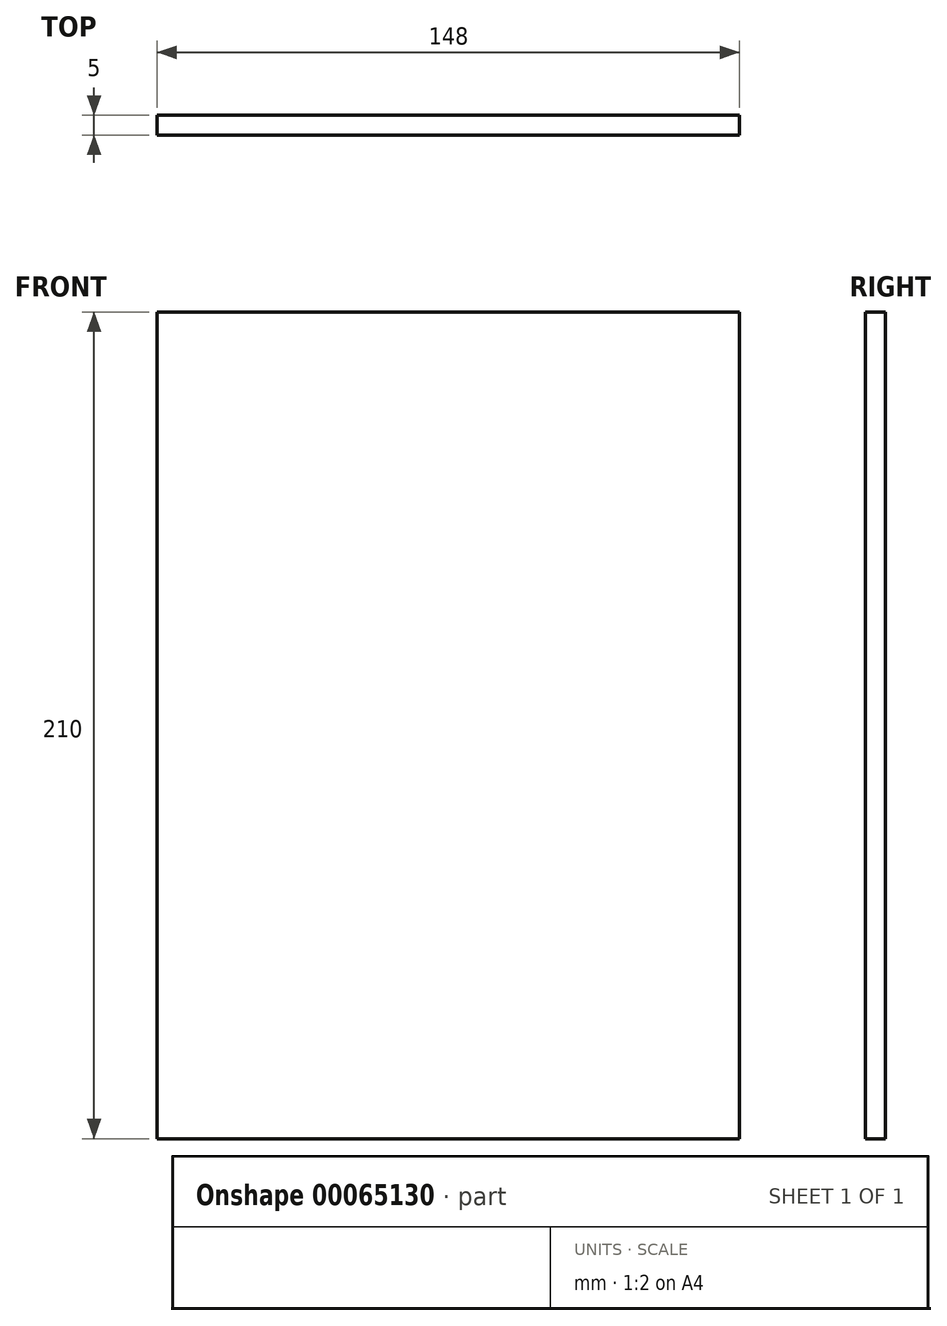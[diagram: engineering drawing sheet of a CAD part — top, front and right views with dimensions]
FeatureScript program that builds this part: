
annotation { "Feature Type Name" : "Feature", "Feature Type Description" : "" }
export const myFeature = defineFeature(function(context is Context, id is Id, definition is map)
    precondition{}
    {
        {
            var Q0;
            Q0=qCreatedBy(makeId("Front.planeOp"),FACE);
            var sketch = newSketch(context, id + "F0", { "sketchPlane" : qUnion([Q0])});
            skLineSegment(sketch, "E0.bottom", {"start": v(0, 0) * mm, "end": v(148, 0) * mm});
            skLineSegment(sketch, "E0.top", {"start": v(0, 210) * mm, "end": v(148, 210) * mm});
            skLineSegment(sketch, "E0.left", {"start": v(0, 0) * mm, "end": v(0, 210) * mm});
            skLineSegment(sketch, "E0.right", {"start": v(148, 0) * mm, "end": v(148, 210) * mm});
            skSolve(sketch);
        }
        {
            var Q0;
            Q0=makeQuery(id+"F0.imprint","IMPRINT",FACE,{"disambiguationData":[TD([[makeQuery(id+"F0.imprint","IMPRINT",EDGE,{"derivedFrom":sQuery(id+"F0.wireOp",EDGE,"E0.bottom")}),1.0]])]});
            extrude(context, id + "F1", {"entities" : qUnion([Q0]), "depth" : 5 * mm});
        }
    });
